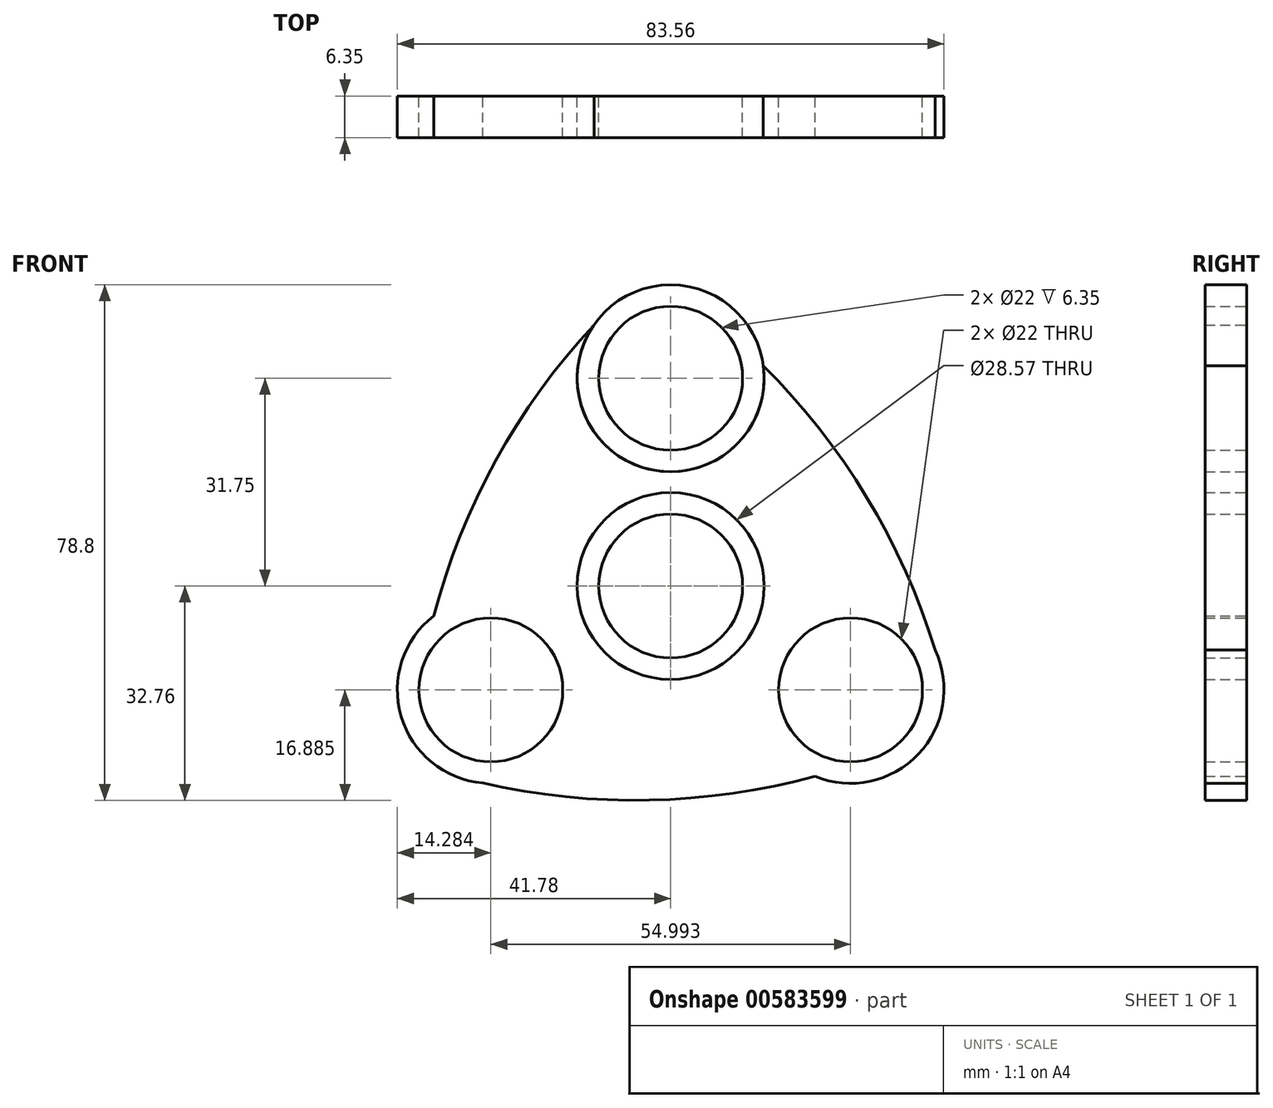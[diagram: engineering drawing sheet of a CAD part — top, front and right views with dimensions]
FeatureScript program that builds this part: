
annotation { "Feature Type Name" : "Feature", "Feature Type Description" : "" }
export const myFeature = defineFeature(function(context is Context, id is Id, definition is map)
    precondition{}
    {
        {
            var Q0;
            Q0=qCreatedBy(makeId("Front.planeOp"),FACE);
            var sketch = newSketch(context, id + "F0", { "sketchPlane" : qUnion([Q0])});
            skCircle(sketch, "E0", {"center": v(0, 31.75) * mm, "radius": 11 * mm});
            skCircle(sketch, "E1", {"center": v(0, 31.75) * mm, "radius": 14.29 * mm});
            skCircle(sketch, "E2", {"center": v(0, 0) * mm, "radius": 11 * mm});
            skCircle(sketch, "E3", {"center": v(0, 0) * mm, "radius": 14.29 * mm});
            skCircle(sketch, "E4.1.0", {"center": v(-27.5, -15.87) * mm, "radius": 11 * mm});
            skCircle(sketch, "E4.1.1", {"center": v(-27.5, -15.87) * mm, "radius": 14.29 * mm});
            skCircle(sketch, "E4.2.0", {"center": v(27.5, -15.88) * mm, "radius": 11 * mm});
            skCircle(sketch, "E4.2.1", {"center": v(27.5, -15.88) * mm, "radius": 14.29 * mm});
            skSolve(sketch);
        }
        {
            var Q0;
            Q0=makeQuery(id+"F0.imprint","IMPRINT",FACE,{"disambiguationData":[TD([[makeQuery(id+"F0.imprint","IMPRINT",EDGE,{"derivedFrom":sQuery(id+"F0.wireOp",EDGE,"E0")}),1.0]])]});
            var sketch = newSketch(context, id + "F1", { "sketchPlane" : qUnion([Q0])});
            skCircle(sketch, "E5.0.0", {"center": v(0, 31.75) * mm, "radius": 14.29 * mm});
            skCircle(sketch, "E6.0", {"center": v(0, 0) * mm, "radius": 14.29 * mm});
            skCircle(sketch, "E7.0", {"center": v(27.5, -15.88) * mm, "radius": 14.29 * mm});
            skCircle(sketch, "E8.0", {"center": v(-27.5, -15.87) * mm, "radius": 14.29 * mm});
            skArc(sketch, "E9", {"start": v(-11.73, 39.91) * mm, "mid": v(-26.72, 19.2) * mm, "end": v(-36.22, -4.56) * mm});
            skArc(sketch, "E10.1.0", {"start": v(-28.7, -30.11) * mm, "mid": v(-3.26, -32.73) * mm, "end": v(22.05, -29.09) * mm});
            skArc(sketch, "E10.2.0", {"start": v(40.43, -9.8) * mm, "mid": v(29.98, 13.54) * mm, "end": v(14.16, 33.64) * mm});
            skCircle(sketch, "E11", {"center": v(0, 0) * mm, "radius": 11 * mm});
            skCircle(sketch, "E12", {"center": v(0, 31.75) * mm, "radius": 11 * mm});
            skCircle(sketch, "E13", {"center": v(-27.5, -15.87) * mm, "radius": 11 * mm});
            skCircle(sketch, "E14", {"center": v(27.5, -15.88) * mm, "radius": 11 * mm});
            skSolve(sketch);
        }
        {
            var Q0;
            Q0=makeQuery(id+"F0.imprint","IMPRINT",FACE,{"disambiguationData":[TD([[makeQuery(id+"F0.imprint","IMPRINT",EDGE,{"derivedFrom":sQuery(id+"F0.wireOp",EDGE,"E0")}),-1.0]])]});
            var Q1;
            Q1=makeQuery(id+"F0.imprint","IMPRINT",FACE,{"disambiguationData":[TD([[makeQuery(id+"F0.imprint","IMPRINT",EDGE,{"derivedFrom":sQuery(id+"F0.wireOp",EDGE,"E2")}),-1.0]])]});
            var Q2;
            Q2=makeQuery(id+"F1.imprint","IMPRINT",FACE,{"disambiguationData":[TD([[makeQuery(id+"F1.imprint","IMPRINT",EDGE,{"derivedFrom":sQuery(id+"F1.wireOp",EDGE,"E14")}),-1.0]])]});
            var Q3;
            Q3=makeQuery(id+"F1.imprint","IMPRINT",FACE,{"disambiguationData":[TD([[makeQuery(id+"F1.imprint","IMPRINT",EDGE,{"derivedFrom":sQuery(id+"F1.wireOp",EDGE,"E13")}),-1.0]])]});
            var Q4;
            Q4=makeQuery(id+"F1.imprint","IMPRINT",FACE,{"disambiguationData":[TD([[makeQuery(id+"F1.imprint","IMPRINT",EDGE,{"derivedFrom":sQuery(id+"F1.wireOp",EDGE,"E6.0")}),-1.0]])]});
            extrude(context, id + "F2", {"entities" : qUnion([Q0, Q1, Q2, Q3, Q4]), "depth" : 6.35 * mm, "offsetDistance" : 25.4 * mm});
        }
    });
